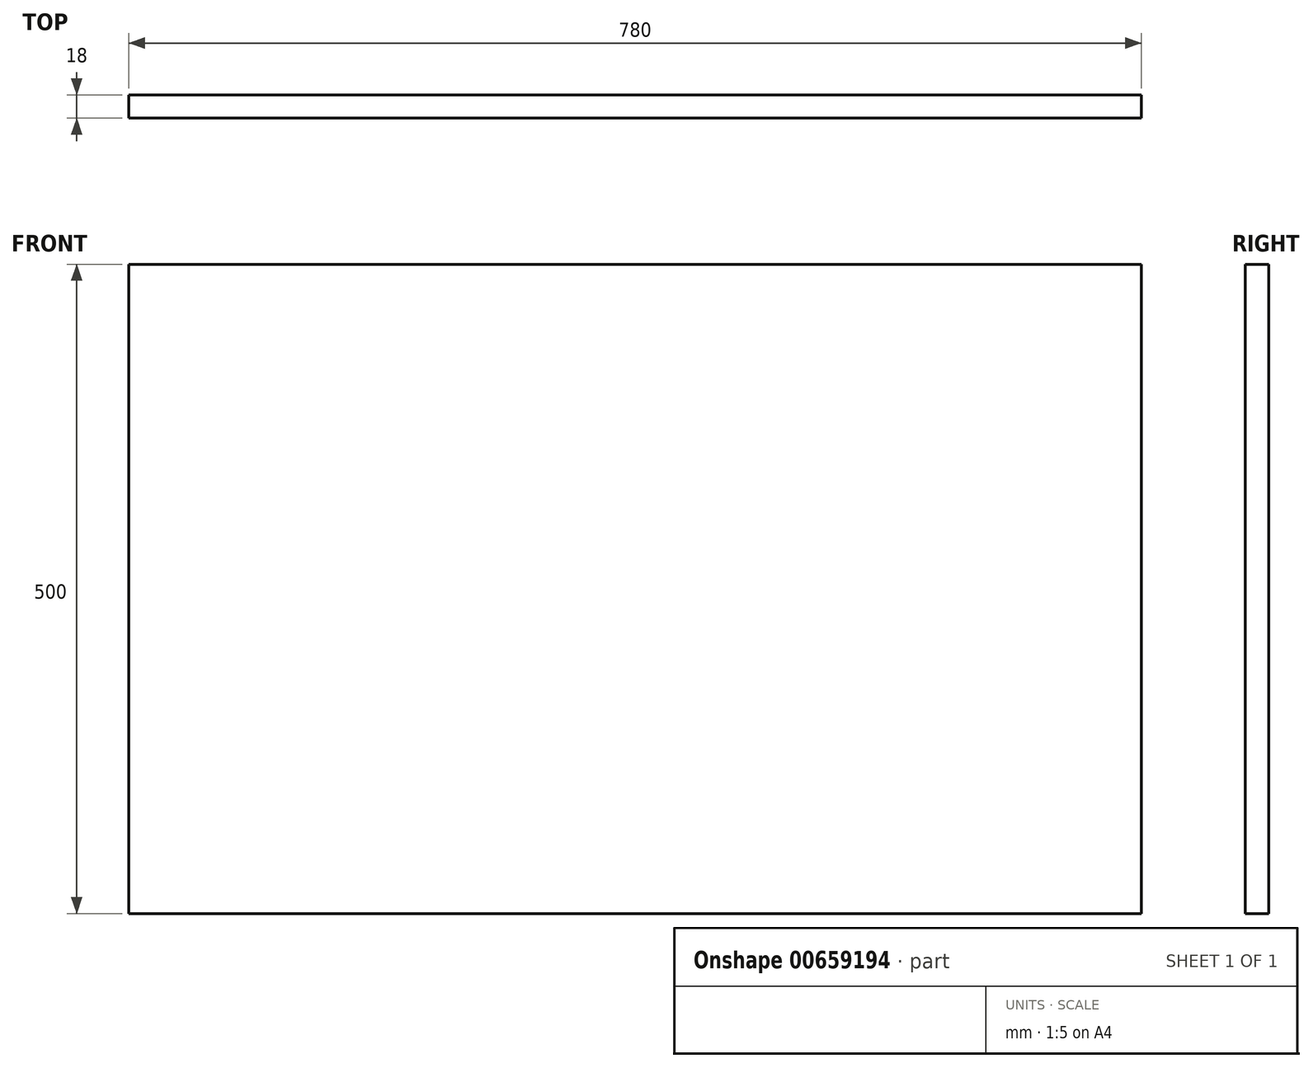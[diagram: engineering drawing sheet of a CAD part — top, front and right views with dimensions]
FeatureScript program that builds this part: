
annotation { "Feature Type Name" : "Feature", "Feature Type Description" : "" }
export const myFeature = defineFeature(function(context is Context, id is Id, definition is map)
    precondition{}
    {
        {
            var Q0;
            Q0=qCreatedBy(makeId("Front.planeOp"),FACE);
            var sketch = newSketch(context, id + "F0", { "sketchPlane" : qUnion([Q0])});
            skLineSegment(sketch, "E0.bottom", {"start": v(458.73, -233.48) * mm, "end": v(-321.27, -233.48) * mm});
            skLineSegment(sketch, "E0.top", {"start": v(458.73, 266.52) * mm, "end": v(-321.27, 266.52) * mm});
            skLineSegment(sketch, "E0.left", {"start": v(458.73, -233.48) * mm, "end": v(458.73, 266.52) * mm});
            skLineSegment(sketch, "E0.right", {"start": v(-321.27, -233.48) * mm, "end": v(-321.27, 266.52) * mm});
            skPoint(sketch, "E0.middle", {"position": v(68.73, 16.52) * mm});
            skSolve(sketch);
        }
        {
            var Q0;
            Q0=makeQuery(id+"F0.imprint","IMPRINT",FACE,{"disambiguationData":[TD([[makeQuery(id+"F0.imprint","IMPRINT",EDGE,{"derivedFrom":sQuery(id+"F0.wireOp",EDGE,"E0.bottom")}),-1.0]])]});
            extrude(context, id + "F1", {"entities" : qUnion([Q0]), "endBound" : BoundingType.SYMMETRIC, "depth" : 18 * mm, "offsetDistance" : 25 * mm});
        }
    });
